# Revit family: Allure B-13 Barstool
name_source: partatom
category: Furniture
revit_build: Autodesk Revit 2017 (Build: 20160225_1515(x64)
units: mm (PartAtom-declared; Revit-internal decimal feet)

## family parameters
Always vertical = Yes
Cut with Voids When Loaded = No
OmniClass Number = 23.40.20.00
OmniClass Title = General Furniture and Specialties
Room Calculation Point = No
Shared = No
Work Plane-Based = No

## types (1)
- Allure B-13 Barstool
    Assembly Code = E2020200
    Assistance = Call for assistance number: 336.941.3446
    Barstool type = Swivel
    Collection = Allure
    Depth = 20 mm  [stored 0.0656168 ft]
    Description = Barstool fully upholstered with swivel base
    Height = 40 mm  [stored 0.131234 ft]
    Industry = Café, Restaurant, Bistro, Hotel,
    Length = 21 mm  [stored 0.0688976 ft]
    Manufacturer = Beaufurn
    Manufacturer Country = Italy
    Model = Allure B-13 Barstool
    Products of collection = Allure Barstools, Allure Chairs and Allure Armchairs
    Seat height = 31 mm  [stored 0.101706 ft]
    Structure material = Steel
    Type Comments = Allure is perfect for guest rooms, offices, lobbies, restaurants and public spaces
    URL = http://beaufurn.com
    Upholstery material = Graded Fabric or Com
    Usage = Indoor
    Yardage = 2 mm  [stored 0.00656168 ft]

note: [stored X ft] marks values corroborated as IEEE doubles in the binary element streams (Revit-internal decimal feet)

## geometry (parser evidence)
native form markers: Sweep x2
no freeform markers — native parametric forms only
